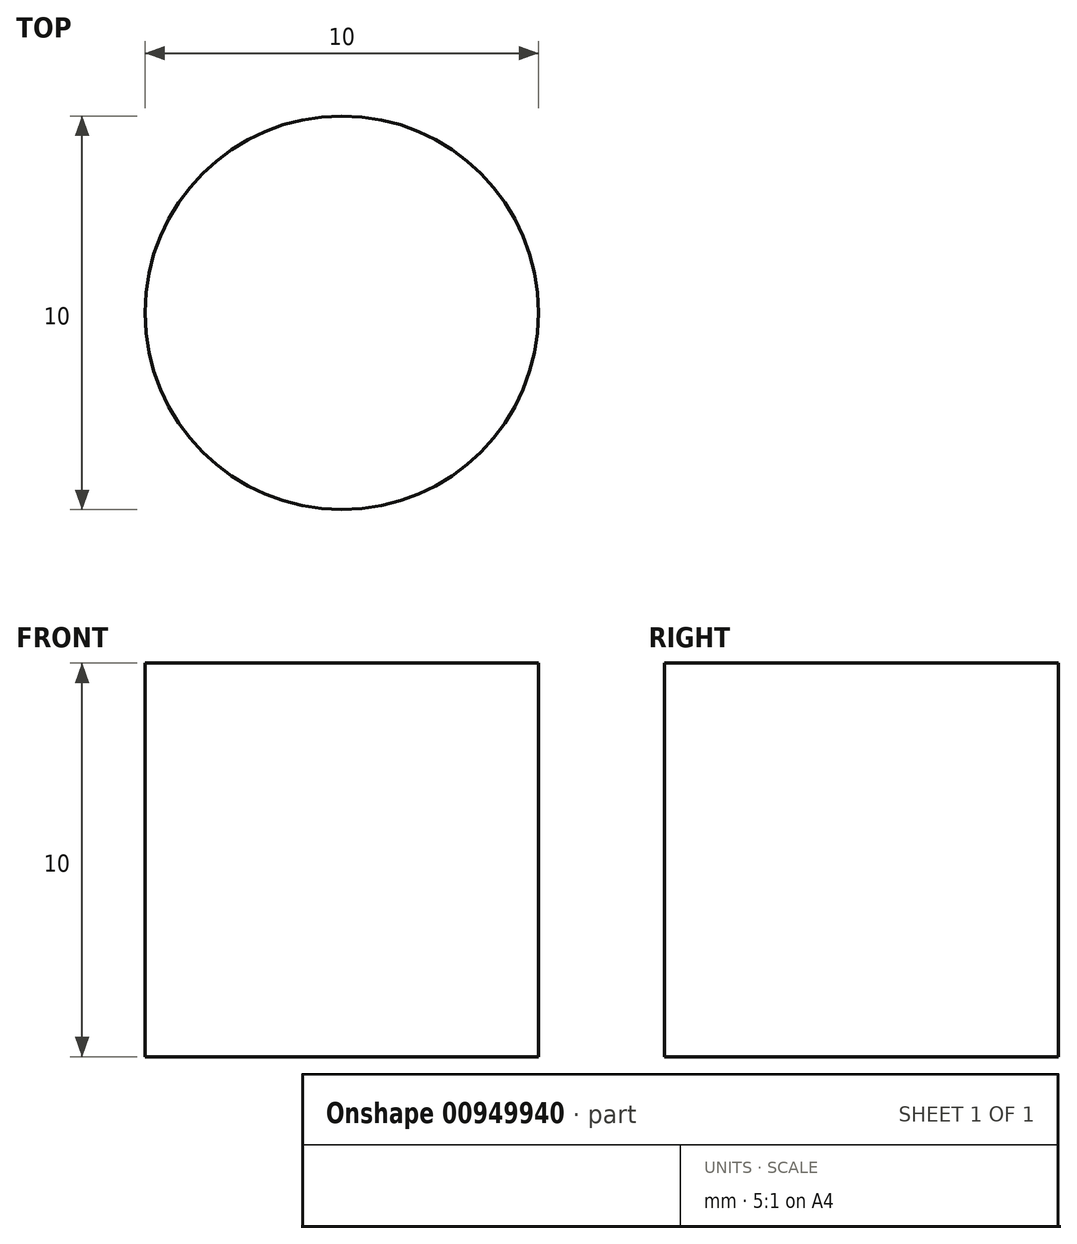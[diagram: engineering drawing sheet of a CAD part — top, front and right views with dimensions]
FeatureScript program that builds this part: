
annotation { "Feature Type Name" : "Feature", "Feature Type Description" : "" }
export const myFeature = defineFeature(function(context is Context, id is Id, definition is map)
    precondition{}
    {
        {
            var Q0;
            Q0=qCreatedBy(makeId("Top.planeOp"),FACE);
            var sketch = newSketch(context, id + "F0", { "sketchPlane" : qUnion([Q0])});
            skCircle(sketch, "E0", {"center": v(0, 0) * mm, "radius": 5 * mm});
            skSolve(sketch);
        }
        {
            var Q0;
            Q0=makeQuery(id+"F0.imprint","IMPRINT",FACE,{"disambiguationData":[TD([[makeQuery(id+"F0.imprint","IMPRINT",EDGE,{"derivedFrom":sQuery(id+"F0.wireOp",EDGE,"E0")}),1.0]])]});
            extrude(context, id + "F1", {"entities" : qUnion([Q0]), "depth" : 10 * mm, "offsetDistance" : 25 * mm});
        }
    });
